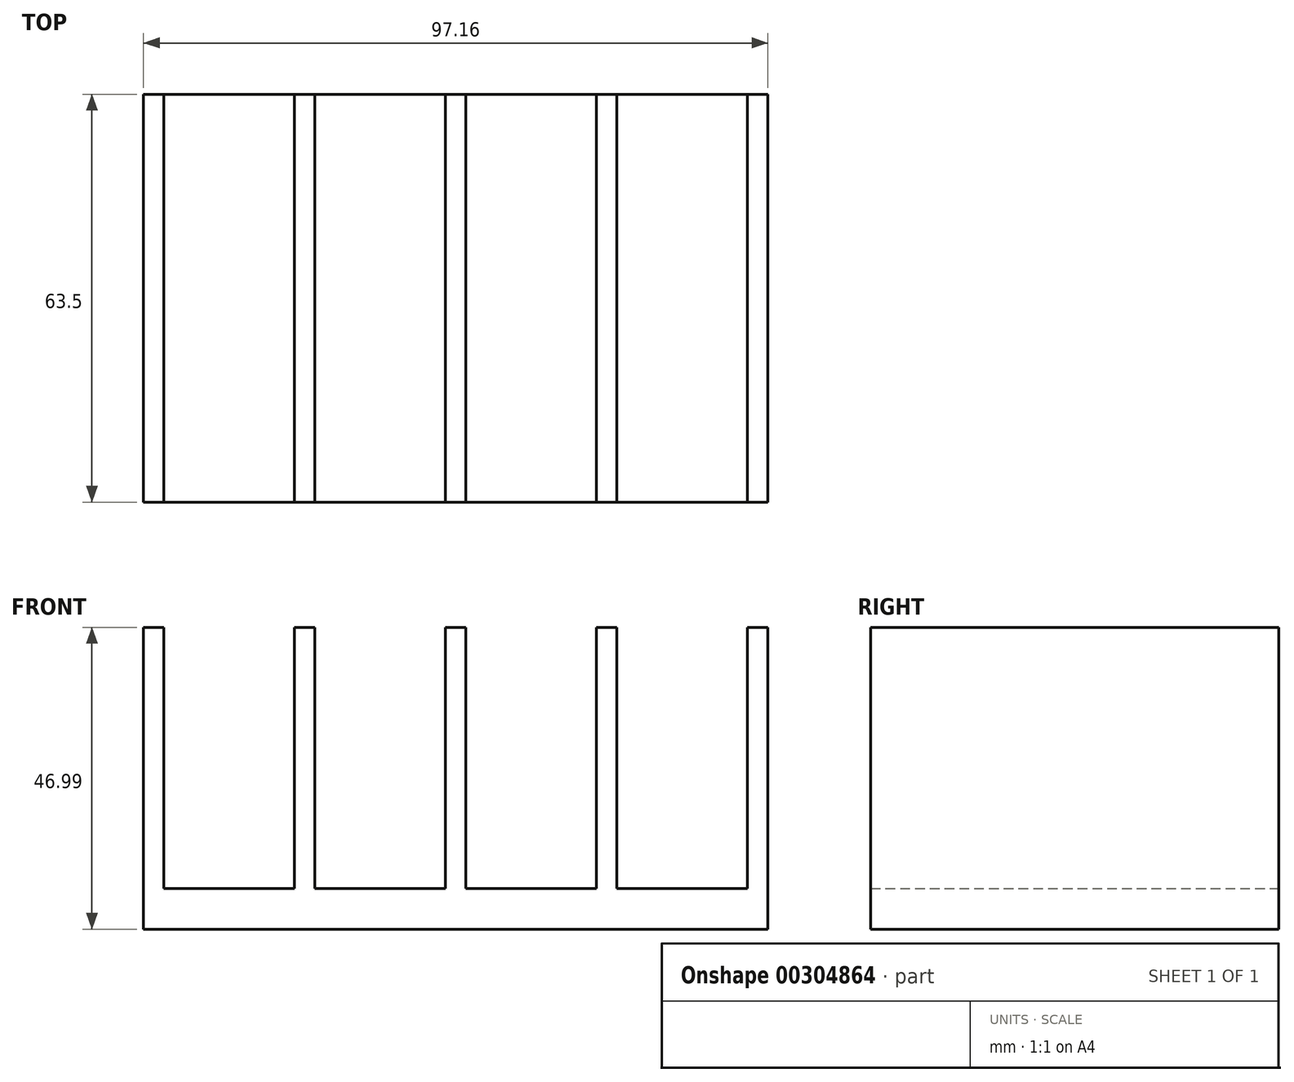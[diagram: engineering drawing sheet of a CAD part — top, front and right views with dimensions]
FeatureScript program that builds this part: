
annotation { "Feature Type Name" : "Feature", "Feature Type Description" : "" }
export const myFeature = defineFeature(function(context is Context, id is Id, definition is map)
    precondition{}
    {
        {
            var Q0;
            Q0=qCreatedBy(makeId("Front.planeOp"),FACE);
            var sketch = newSketch(context, id + "F0", { "sketchPlane" : qUnion([Q0])});
            skLineSegment(sketch, "E0.bottom", {"start": v(48.58, 3.18) * mm, "end": v(-48.58, 3.18) * mm});
            skLineSegment(sketch, "E0.top", {"start": v(48.58, -3.18) * mm, "end": v(-48.58, -3.18) * mm});
            skLineSegment(sketch, "E0.left", {"start": v(48.58, 3.18) * mm, "end": v(48.58, -3.18) * mm});
            skLineSegment(sketch, "E0.right", {"start": v(-48.58, 3.18) * mm, "end": v(-48.58, -3.18) * mm});
            skPoint(sketch, "E0.middle", {"position": v(0, 0) * mm});
            skLineSegment(sketch, "E1.bottom", {"start": v(-48.58, 3.18) * mm, "end": v(-45.4, 3.18) * mm});
            skLineSegment(sketch, "E1.top", {"start": v(-48.58, 43.82) * mm, "end": v(-45.4, 43.82) * mm});
            skLineSegment(sketch, "E1.left", {"start": v(-48.58, 3.18) * mm, "end": v(-48.58, 43.82) * mm});
            skLineSegment(sketch, "E1.right", {"start": v(-45.4, 3.18) * mm, "end": v(-45.4, 43.82) * mm});
            skLineSegment(sketch, "E2.bottom", {"start": v(-25.08, 3.18) * mm, "end": v(-21.9, 3.18) * mm});
            skLineSegment(sketch, "E2.top", {"start": v(-25.08, 43.82) * mm, "end": v(-21.9, 43.82) * mm});
            skLineSegment(sketch, "E2.left", {"start": v(-25.08, 3.17) * mm, "end": v(-25.08, 43.81) * mm});
            skLineSegment(sketch, "E2.right", {"start": v(-21.9, 3.17) * mm, "end": v(-21.9, 43.81) * mm});
            skLineSegment(sketch, "E3.bottom", {"start": v(-1.59, 3.18) * mm, "end": v(1.59, 3.18) * mm});
            skLineSegment(sketch, "E3.top", {"start": v(-1.59, 43.82) * mm, "end": v(1.59, 43.82) * mm});
            skLineSegment(sketch, "E3.left", {"start": v(-1.59, 3.17) * mm, "end": v(-1.59, 43.81) * mm});
            skLineSegment(sketch, "E3.right", {"start": v(1.59, 3.17) * mm, "end": v(1.59, 43.81) * mm});
            skLineSegment(sketch, "E4.bottom", {"start": v(21.9, 3.18) * mm, "end": v(25.08, 3.18) * mm});
            skLineSegment(sketch, "E4.top", {"start": v(21.9, 43.82) * mm, "end": v(25.08, 43.82) * mm});
            skLineSegment(sketch, "E4.left", {"start": v(21.9, 3.17) * mm, "end": v(21.9, 43.81) * mm});
            skLineSegment(sketch, "E4.right", {"start": v(25.08, 3.17) * mm, "end": v(25.08, 43.81) * mm});
            skLineSegment(sketch, "E5.bottom", {"start": v(48.58, 3.18) * mm, "end": v(48.58, 3.18) * mm});
            skLineSegment(sketch, "E6.bottom", {"start": v(48.58, 3.18) * mm, "end": v(45.4, 3.18) * mm});
            skLineSegment(sketch, "E6.top", {"start": v(48.58, 43.82) * mm, "end": v(45.4, 43.82) * mm});
            skLineSegment(sketch, "E6.left", {"start": v(48.58, 3.18) * mm, "end": v(48.58, 43.82) * mm});
            skLineSegment(sketch, "E6.right", {"start": v(45.4, 3.18) * mm, "end": v(45.4, 43.82) * mm});
            skSolve(sketch);
        }
        {
            var Q0;
            Q0=qSketchRegion(id+"F0",true);
            extrude(context, id + "F1", {"entities" : qUnion([Q0]), "depth" : 63.5 * mm});
        }
    });
